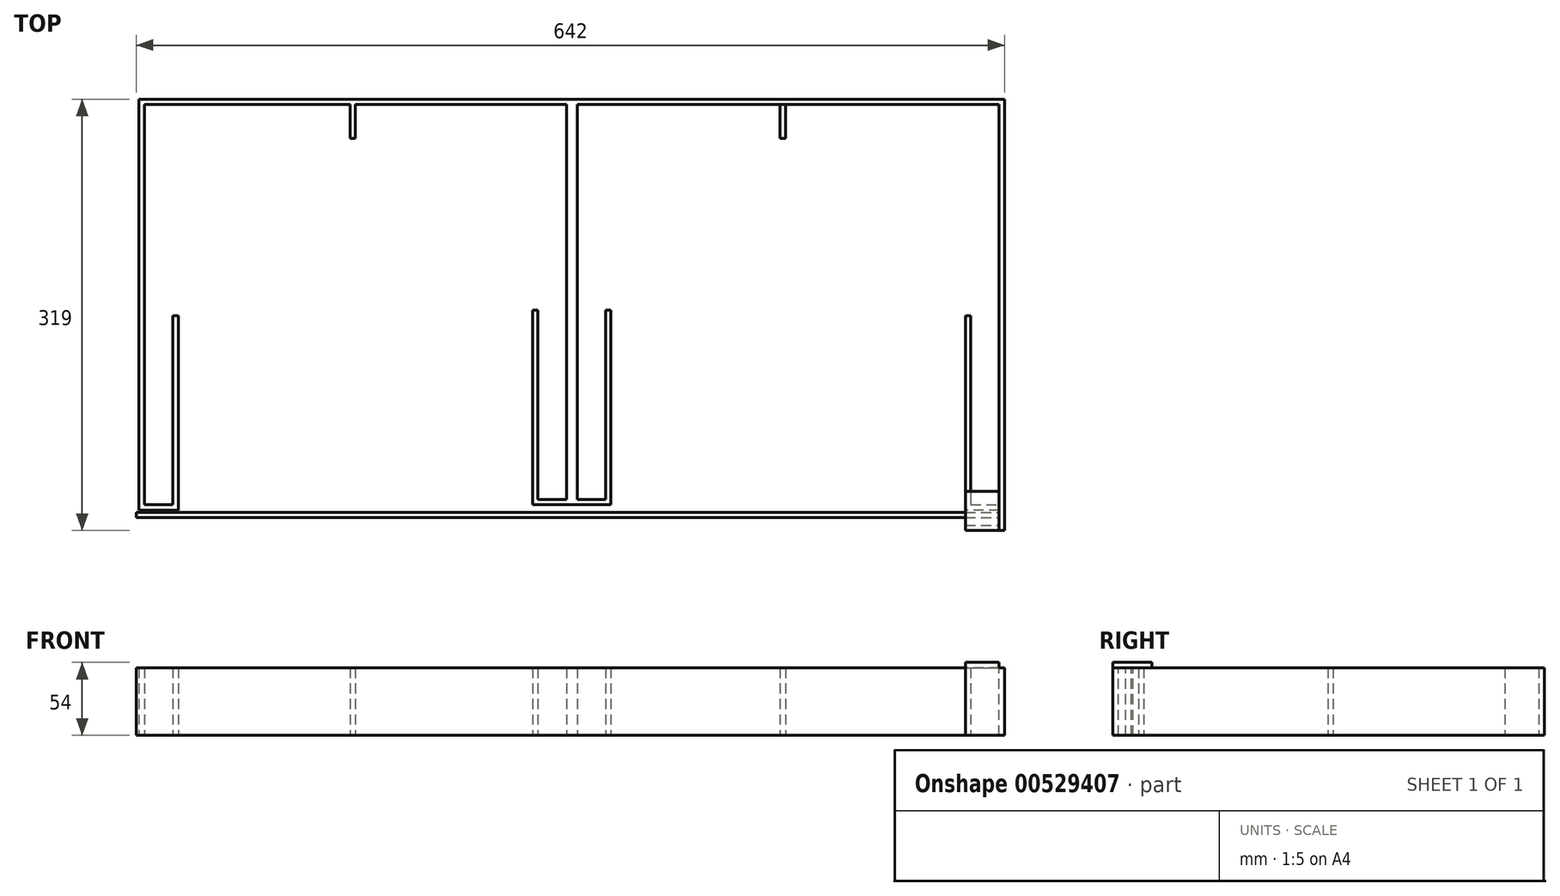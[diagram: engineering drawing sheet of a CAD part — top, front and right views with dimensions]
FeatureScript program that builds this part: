
annotation { "Feature Type Name" : "Feature", "Feature Type Description" : "" }
export const myFeature = defineFeature(function(context is Context, id is Id, definition is map)
    precondition{}
    {
        {
            var Q0;
            Q0=qCreatedBy(makeId("Front.planeOp"),FACE);
            var sketch = newSketch(context, id + "F0", { "sketchPlane" : qUnion([Q0])});
            skLineSegment(sketch, "E0.bottom", {"start": v(320, 25) * mm, "end": v(-320, 25) * mm});
            skLineSegment(sketch, "E0.top", {"start": v(320, -25) * mm, "end": v(-320, -25) * mm});
            skLineSegment(sketch, "E0.left", {"start": v(320, 25) * mm, "end": v(320, -25) * mm});
            skLineSegment(sketch, "E0.right", {"start": v(-320, 25) * mm, "end": v(-320, -25) * mm});
            skPoint(sketch, "E0.middle", {"position": v(0, 0) * mm});
            skSolve(sketch);
        }
        {
            var Q0;
            Q0=makeQuery(id+"F0.imprint","IMPRINT",FACE,{"disambiguationData":[TD([[makeQuery(id+"F0.imprint","IMPRINT",EDGE,{"derivedFrom":sQuery(id+"F0.wireOp",EDGE,"E0.bottom")}),1.0]])]});
            extrude(context, id + "F1", {"entities" : qUnion([Q0]), "depth" : 4 * mm, "offsetDistance" : 25 * mm});
        }
        {
            var Q0;
            Q0=makeQuery(id+"F1.opExtrude","CAP_FACE",FACE,{"disambiguationData":[OSD([sQuery(id+"F0.wireOp",EDGE,"E0.bottom"),sQuery(id+"F0.wireOp",EDGE,"E0.top"),sQuery(id+"F0.wireOp",EDGE,"E0.left"),sQuery(id+"F0.wireOp",EDGE,"E0.right")])],"isStart":false});
            var sketch = newSketch(context, id + "F2", { "sketchPlane" : qUnion([Q0])});
            skLineSegment(sketch, "E1.bottom", {"start": v(-320, 25) * mm, "end": v(-316, 25) * mm});
            skLineSegment(sketch, "E1.top", {"start": v(-320, -25) * mm, "end": v(-316, -25) * mm});
            skLineSegment(sketch, "E1.left", {"start": v(-320, 25) * mm, "end": v(-320, -25) * mm});
            skLineSegment(sketch, "E1.right", {"start": v(-316, 25) * mm, "end": v(-316, -25) * mm});
            skSolve(sketch);
        }
        {
            var Q0;
            Q0 = qSketchRegion(id + "F2", true);
            extrude(context, id + "F3", {"entities" : qUnion([Q0]), "operationType" : NewBodyOperationType.ADD, "depth" : 300 * mm, "offsetDistance" : 25 * mm});
        }
        {
            var Q0;
            Q0=makeQuery(id+"F1.opExtrude","CAP_FACE",FACE,{"disambiguationData":[OSD([sQuery(id+"F0.wireOp",EDGE,"E0.bottom"),sQuery(id+"F0.wireOp",EDGE,"E0.top"),sQuery(id+"F0.wireOp",EDGE,"E0.left"),sQuery(id+"F0.wireOp",EDGE,"E0.right")])],"isStart":false});
            var sketch = newSketch(context, id + "F4", { "sketchPlane" : qUnion([Q0])});
            skLineSegment(sketch, "E2.bottom", {"start": v(320, -25) * mm, "end": v(316, -25) * mm});
            skLineSegment(sketch, "E2.top", {"start": v(320, 25) * mm, "end": v(316, 25) * mm});
            skLineSegment(sketch, "E2.left", {"start": v(320, -25) * mm, "end": v(320, 25) * mm});
            skLineSegment(sketch, "E2.right", {"start": v(316, -25) * mm, "end": v(316, 25) * mm});
            skSolve(sketch);
        }
        {
            var Q0;
            Q0 = qSketchRegion(id + "F4", true);
            extrude(context, id + "F5", {"entities" : qUnion([Q0]), "operationType" : NewBodyOperationType.ADD, "depth" : 300 * mm, "offsetDistance" : 25 * mm});
        }
        {
            var Q0;
            Q0=makeQuery(id+"F3.opExtrude","SWEPT_FACE",FACE,{"disambiguationData":[OSD([sQuery(id+"F2.wireOp",EDGE,"E1.right")])]});
            var sketch = newSketch(context, id + "F6", { "sketchPlane" : qUnion([Q0])});
            skLineSegment(sketch, "E3.bottom", {"start": v(-304, 25) * mm, "end": v(-300, 25) * mm});
            skLineSegment(sketch, "E3.top", {"start": v(-304, -25) * mm, "end": v(-300, -25) * mm});
            skLineSegment(sketch, "E3.left", {"start": v(-304, 25) * mm, "end": v(-304, -25) * mm});
            skLineSegment(sketch, "E3.right", {"start": v(-300, 25) * mm, "end": v(-300, -25) * mm});
            skSolve(sketch);
        }
        {
            var Q0;
            Q0 = qSketchRegion(id + "F6", true);
            extrude(context, id + "F7", {"entities" : qUnion([Q0]), "operationType" : NewBodyOperationType.ADD, "depth" : 25 * mm, "offsetDistance" : 25 * mm});
        }
        {
            var Q0;
            Q0=makeQuery(id+"F5.opExtrude","SWEPT_FACE",FACE,{"disambiguationData":[OSD([sQuery(id+"F4.wireOp",EDGE,"E2.right")])]});
            var sketch = newSketch(context, id + "F8", { "sketchPlane" : qUnion([Q0])});
            skLineSegment(sketch, "E4.bottom", {"start": v(304, 25) * mm, "end": v(300, 25) * mm});
            skLineSegment(sketch, "E4.top", {"start": v(304, -25) * mm, "end": v(300, -25) * mm});
            skLineSegment(sketch, "E4.left", {"start": v(304, 25) * mm, "end": v(304, -25) * mm});
            skLineSegment(sketch, "E4.right", {"start": v(300, 25) * mm, "end": v(300, -25) * mm});
            skSolve(sketch);
        }
        {
            var Q0;
            Q0 = qSketchRegion(id + "F8", true);
            extrude(context, id + "F9", {"entities" : qUnion([Q0]), "operationType" : NewBodyOperationType.ADD, "depth" : 25 * mm, "offsetDistance" : 25 * mm});
        }
        {
            var Q0;
            Q0=qCreatedBy(makeId("Front.planeOp"),FACE);
            var sketch = newSketch(context, id + "F10", { "sketchPlane" : qUnion([Q0])});
            skLineSegment(sketch, "E5.bottom", {"start": v(4, 25) * mm, "end": v(-4, 25) * mm});
            skLineSegment(sketch, "E5.top", {"start": v(4, -25) * mm, "end": v(-4, -25) * mm});
            skLineSegment(sketch, "E5.left", {"start": v(4, 25) * mm, "end": v(4, -25) * mm});
            skLineSegment(sketch, "E5.right", {"start": v(-4, 25) * mm, "end": v(-4, -25) * mm});
            skPoint(sketch, "E5.middle", {"position": v(0, 0) * mm});
            skSolve(sketch);
        }
        {
            var Q0;
            Q0 = qSketchRegion(id + "F10", true);
            extrude(context, id + "F11", {"entities" : qUnion([Q0]), "operationType" : NewBodyOperationType.ADD, "depth" : 300 * mm, "offsetDistance" : 25 * mm});
        }
        {
            var Q0;
            {var subQ0=sQuery(id+"F0.wireOp",EDGE,"E0.bottom");var subQ1=sQuery(id+"F0.wireOp",EDGE,"E0.top");Q0=makeQuery(id+"F11.boolean.opBoolean","SPLIT",FACE,{"disambiguationData":[TD([makeQuery(id+"F3.opExtrude","SWEPT_FACE",FACE,{"disambiguationData":[OSD([sQuery(id+"F2.wireOp",EDGE,"E1.right")])]})])],"derivedFrom":makeQuery(id+"F1.opExtrude","CAP_FACE",FACE,{"disambiguationData":[OSD([subQ0,subQ1,sQuery(id+"F0.wireOp",EDGE,"E0.left"),sQuery(id+"F0.wireOp",EDGE,"E0.right")])],"isStart":false})});}
            var sketch = newSketch(context, id + "F12", { "sketchPlane" : qUnion([Q0])});
            skLineSegment(sketch, "E6.bottom", {"start": v(-160, 25) * mm, "end": v(-164, 25) * mm});
            skLineSegment(sketch, "E6.top", {"start": v(-160, -25) * mm, "end": v(-164, -25) * mm});
            skLineSegment(sketch, "E6.left", {"start": v(-160, 25) * mm, "end": v(-160, -25) * mm});
            skLineSegment(sketch, "E6.right", {"start": v(-164, 25) * mm, "end": v(-164, -25) * mm});
            skSolve(sketch);
        }
        {
            var Q0;
            Q0=makeQuery(id+"F12.imprint","IMPRINT",FACE,{"disambiguationData":[TD([[makeQuery(id+"F12.imprint","IMPRINT",EDGE,{"derivedFrom":sQuery(id+"F12.wireOp",EDGE,"E6.bottom")}),1.0]])]});
            extrude(context, id + "F13", {"entities" : qUnion([Q0]), "operationType" : NewBodyOperationType.ADD, "depth" : 25 * mm, "offsetDistance" : 25 * mm});
        }
        {
            var Q0;
            Q0=makeQuery(id+"F11.opExtrude","SWEPT_FACE",FACE,{"disambiguationData":[OSD([sQuery(id+"F10.wireOp",EDGE,"E5.right")])]});
            var sketch = newSketch(context, id + "F14", { "sketchPlane" : qUnion([Q0])});
            skLineSegment(sketch, "E7.bottom", {"start": v(300, 25) * mm, "end": v(296, 25) * mm});
            skLineSegment(sketch, "E7.top", {"start": v(300, -25) * mm, "end": v(296, -25) * mm});
            skLineSegment(sketch, "E7.left", {"start": v(300, 25) * mm, "end": v(300, -25) * mm});
            skLineSegment(sketch, "E7.right", {"start": v(296, 25) * mm, "end": v(296, -25) * mm});
            skSolve(sketch);
        }
        {
            var Q0;
            Q0 = qSketchRegion(id + "F14", true);
            extrude(context, id + "F15", {"entities" : qUnion([Q0]), "operationType" : NewBodyOperationType.ADD, "depth" : 25 * mm, "offsetDistance" : 25 * mm});
        }
        {
            var Q0;
            Q0=makeQuery(id+"F7.opExtrude","SWEPT_FACE",FACE,{"disambiguationData":[OSD([sQuery(id+"F6.wireOp",EDGE,"E3.right")])]});
            var sketch = newSketch(context, id + "F16", { "sketchPlane" : qUnion([Q0])});
            skLineSegment(sketch, "E8.bottom", {"start": v(291, 25) * mm, "end": v(295, 25) * mm});
            skLineSegment(sketch, "E8.top", {"start": v(291, -25) * mm, "end": v(295, -25) * mm});
            skLineSegment(sketch, "E8.left", {"start": v(291, 25) * mm, "end": v(291, -25) * mm});
            skLineSegment(sketch, "E8.right", {"start": v(295, 25) * mm, "end": v(295, -25) * mm});
            skSolve(sketch);
        }
        {
            var Q0;
            Q0 = qSketchRegion(id + "F16", true);
            extrude(context, id + "F17", {"entities" : qUnion([Q0]), "operationType" : NewBodyOperationType.ADD, "depth" : 140 * mm, "offsetDistance" : 25 * mm});
        }
        {
            var Q0;
            Q0=makeQuery(id+"F15.opExtrude","SWEPT_FACE",FACE,{"disambiguationData":[OSD([sQuery(id+"F14.wireOp",EDGE,"E7.right")])]});
            var sketch = newSketch(context, id + "F18", { "sketchPlane" : qUnion([Q0])});
            skLineSegment(sketch, "E9.bottom", {"start": v(29, 25) * mm, "end": v(25, 25) * mm});
            skLineSegment(sketch, "E9.top", {"start": v(29, -25) * mm, "end": v(25, -25) * mm});
            skLineSegment(sketch, "E9.left", {"start": v(29, 25) * mm, "end": v(29, -25) * mm});
            skLineSegment(sketch, "E9.right", {"start": v(25, 25) * mm, "end": v(25, -25) * mm});
            skSolve(sketch);
        }
        {
            var Q0;
            Q0 = qSketchRegion(id + "F18", true);
            extrude(context, id + "F19", {"entities" : qUnion([Q0]), "operationType" : NewBodyOperationType.ADD, "depth" : 140 * mm, "offsetDistance" : 25 * mm});
        }
        {
            var Q0;
            Q0=makeQuery(id+"F19.boolean.opBoolean","MERGE",FACE,{"derivedFrom":[makeQuery(id+"F17.boolean.opBoolean","MERGE",FACE,{"derivedFrom":[makeQuery(id+"F15.boolean.opBoolean","MERGE",FACE,{"derivedFrom":[makeQuery(id+"F13.boolean.opBoolean","MERGE",FACE,{"derivedFrom":[makeQuery(id+"F11.boolean.opBoolean","MERGE",FACE,{"derivedFrom":[makeQuery(id+"F9.boolean.opBoolean","MERGE",FACE,{"derivedFrom":[makeQuery(id+"F7.boolean.opBoolean","MERGE",FACE,{"derivedFrom":[makeQuery(id+"F5.boolean.opBoolean","MERGE",FACE,{"derivedFrom":[makeQuery(id+"F3.boolean.opBoolean","MERGE",FACE,{"derivedFrom":[makeQuery(id+"F1.opExtrude","SWEPT_FACE",FACE,{"disambiguationData":[OSD([sQuery(id+"F0.wireOp",EDGE,"E0.bottom")])]}),makeQuery(id+"F3.opExtrude","SWEPT_FACE",FACE,{"disambiguationData":[OSD([sQuery(id+"F2.wireOp",EDGE,"E1.bottom")])]})]}),makeQuery(id+"F5.opExtrude","SWEPT_FACE",FACE,{"disambiguationData":[OSD([sQuery(id+"F4.wireOp",EDGE,"E2.top")])]})]}),makeQuery(id+"F7.opExtrude","SWEPT_FACE",FACE,{"disambiguationData":[OSD([sQuery(id+"F6.wireOp",EDGE,"E3.bottom")])]})]}),makeQuery(id+"F9.opExtrude","SWEPT_FACE",FACE,{"disambiguationData":[OSD([sQuery(id+"F8.wireOp",EDGE,"E4.bottom")])]})]}),makeQuery(id+"F11.opExtrude","SWEPT_FACE",FACE,{"disambiguationData":[OSD([sQuery(id+"F10.wireOp",EDGE,"E5.bottom")])]})]}),makeQuery(id+"F13.opExtrude","SWEPT_FACE",FACE,{"disambiguationData":[OSD([sQuery(id+"F12.wireOp",EDGE,"E6.bottom")])]})]}),makeQuery(id+"F15.opExtrude","SWEPT_FACE",FACE,{"disambiguationData":[OSD([sQuery(id+"F14.wireOp",EDGE,"E7.bottom")])]})]}),makeQuery(id+"F17.opExtrude","SWEPT_FACE",FACE,{"disambiguationData":[OSD([sQuery(id+"F16.wireOp",EDGE,"E8.bottom")])]})]}),makeQuery(id+"F19.opExtrude","SWEPT_FACE",FACE,{"disambiguationData":[OSD([sQuery(id+"F18.wireOp",EDGE,"E9.bottom")])]})]});
            var sketch = newSketch(context, id + "F20", { "sketchPlane" : qUnion([Q0])});
            skArc(sketch, "E10", {"start": v(-25, -156) * mm, "mid": v(-161.91, -28.95) * mm, "end": v(-295, -160) * mm});
            skArc(sketch, "E11", {"start": v(-29, -156) * mm, "mid": v(-161.91, -32.85) * mm, "end": v(-291, -160) * mm});
            skSolve(sketch);
        }
        {
            var Q0;
            Q0=sQuery(id+"F20.wireOp",EDGE,"E11");
            var Q1;
            Q1=sQuery(id+"F20.wireOp",EDGE,"E10");
            extrude(context, id + "F21", {"bodyType" : ToolBodyType.SURFACE, "surfaceEntities" : qUnion([Q0, Q1]), "oppositeDirection" : true, "depth" : 50 * mm, "offsetDistance" : 25 * mm});
        }
        {
            var Q0;
            Q0=makeQuery(id+"F11.opExtrude","SWEPT_FACE",FACE,{"disambiguationData":[OSD([sQuery(id+"F10.wireOp",EDGE,"E5.left")])]});
            var sketch = newSketch(context, id + "F22", { "sketchPlane" : qUnion([Q0])});
            skLineSegment(sketch, "E12.bottom", {"start": v(-300, 25) * mm, "end": v(-296, 25) * mm});
            skLineSegment(sketch, "E12.top", {"start": v(-300, -25) * mm, "end": v(-296, -25) * mm});
            skLineSegment(sketch, "E12.left", {"start": v(-300, 25) * mm, "end": v(-300, -25) * mm});
            skLineSegment(sketch, "E12.right", {"start": v(-296, 25) * mm, "end": v(-296, -25) * mm});
            skSolve(sketch);
        }
        {
            var Q0;
            Q0 = qSketchRegion(id + "F22", true);
            extrude(context, id + "F23", {"entities" : qUnion([Q0]), "operationType" : NewBodyOperationType.ADD, "depth" : 25 * mm, "offsetDistance" : 25 * mm});
        }
        {
            var Q0;
            Q0=makeQuery(id+"F23.opExtrude","SWEPT_FACE",FACE,{"disambiguationData":[OSD([sQuery(id+"F22.wireOp",EDGE,"E12.right")])]});
            var sketch = newSketch(context, id + "F24", { "sketchPlane" : qUnion([Q0])});
            skLineSegment(sketch, "E13.bottom", {"start": v(-29, 25) * mm, "end": v(-25, 25) * mm});
            skLineSegment(sketch, "E13.top", {"start": v(-29, -25) * mm, "end": v(-25, -25) * mm});
            skLineSegment(sketch, "E13.left", {"start": v(-29, 25) * mm, "end": v(-29, -25) * mm});
            skLineSegment(sketch, "E13.right", {"start": v(-25, 25) * mm, "end": v(-25, -25) * mm});
            skSolve(sketch);
        }
        {
            var Q0;
            Q0 = qSketchRegion(id + "F24", true);
            extrude(context, id + "F25", {"entities" : qUnion([Q0]), "operationType" : NewBodyOperationType.ADD, "depth" : 140 * mm, "offsetDistance" : 25 * mm});
        }
        {
            var Q0;
            Q0=makeQuery(id+"F9.opExtrude","SWEPT_FACE",FACE,{"disambiguationData":[OSD([sQuery(id+"F8.wireOp",EDGE,"E4.right")])]});
            var sketch = newSketch(context, id + "F26", { "sketchPlane" : qUnion([Q0])});
            skLineSegment(sketch, "E14.bottom", {"start": v(-291, 25) * mm, "end": v(-295, 25) * mm});
            skLineSegment(sketch, "E14.top", {"start": v(-291, -25) * mm, "end": v(-295, -25) * mm});
            skLineSegment(sketch, "E14.left", {"start": v(-291, 25) * mm, "end": v(-291, -25) * mm});
            skLineSegment(sketch, "E14.right", {"start": v(-295, 25) * mm, "end": v(-295, -25) * mm});
            skSolve(sketch);
        }
        {
            var Q0;
            Q0 = qSketchRegion(id + "F26", true);
            extrude(context, id + "F27", {"entities" : qUnion([Q0]), "operationType" : NewBodyOperationType.ADD, "depth" : 140 * mm, "offsetDistance" : 25 * mm});
        }
        {
            var Q0;
            Q0=makeQuery(id+"F27.boolean.opBoolean","MERGE",FACE,{"derivedFrom":[makeQuery(id+"F25.boolean.opBoolean","MERGE",FACE,{"derivedFrom":[makeQuery(id+"F23.boolean.opBoolean","MERGE",FACE,{"derivedFrom":[makeQuery(id+"F19.boolean.opBoolean","MERGE",FACE,{"derivedFrom":[makeQuery(id+"F17.boolean.opBoolean","MERGE",FACE,{"derivedFrom":[makeQuery(id+"F15.boolean.opBoolean","MERGE",FACE,{"derivedFrom":[makeQuery(id+"F13.boolean.opBoolean","MERGE",FACE,{"derivedFrom":[makeQuery(id+"F11.boolean.opBoolean","MERGE",FACE,{"derivedFrom":[makeQuery(id+"F9.boolean.opBoolean","MERGE",FACE,{"derivedFrom":[makeQuery(id+"F7.boolean.opBoolean","MERGE",FACE,{"derivedFrom":[makeQuery(id+"F5.boolean.opBoolean","MERGE",FACE,{"derivedFrom":[makeQuery(id+"F3.boolean.opBoolean","MERGE",FACE,{"derivedFrom":[makeQuery(id+"F1.opExtrude","SWEPT_FACE",FACE,{"disambiguationData":[OSD([sQuery(id+"F0.wireOp",EDGE,"E0.top")])]}),makeQuery(id+"F3.opExtrude","SWEPT_FACE",FACE,{"disambiguationData":[OSD([sQuery(id+"F2.wireOp",EDGE,"E1.top")])]})]}),makeQuery(id+"F5.opExtrude","SWEPT_FACE",FACE,{"disambiguationData":[OSD([sQuery(id+"F4.wireOp",EDGE,"E2.bottom")])]})]}),makeQuery(id+"F7.opExtrude","SWEPT_FACE",FACE,{"disambiguationData":[OSD([sQuery(id+"F6.wireOp",EDGE,"E3.top")])]})]}),makeQuery(id+"F9.opExtrude","SWEPT_FACE",FACE,{"disambiguationData":[OSD([sQuery(id+"F8.wireOp",EDGE,"E4.top")])]})]}),makeQuery(id+"F11.opExtrude","SWEPT_FACE",FACE,{"disambiguationData":[OSD([sQuery(id+"F10.wireOp",EDGE,"E5.top")])]})]}),makeQuery(id+"F13.opExtrude","SWEPT_FACE",FACE,{"disambiguationData":[OSD([sQuery(id+"F12.wireOp",EDGE,"E6.top")])]})]}),makeQuery(id+"F15.opExtrude","SWEPT_FACE",FACE,{"disambiguationData":[OSD([sQuery(id+"F14.wireOp",EDGE,"E7.top")])]})]}),makeQuery(id+"F17.opExtrude","SWEPT_FACE",FACE,{"disambiguationData":[OSD([sQuery(id+"F16.wireOp",EDGE,"E8.top")])]})]}),makeQuery(id+"F19.opExtrude","SWEPT_FACE",FACE,{"disambiguationData":[OSD([sQuery(id+"F18.wireOp",EDGE,"E9.top")])]})]}),makeQuery(id+"F23.opExtrude","SWEPT_FACE",FACE,{"disambiguationData":[OSD([sQuery(id+"F22.wireOp",EDGE,"E12.top")])]})]}),makeQuery(id+"F25.opExtrude","SWEPT_FACE",FACE,{"disambiguationData":[OSD([sQuery(id+"F24.wireOp",EDGE,"E13.top")])]})]}),makeQuery(id+"F27.opExtrude","SWEPT_FACE",FACE,{"disambiguationData":[OSD([sQuery(id+"F26.wireOp",EDGE,"E14.top")])]})]});
            var sketch = newSketch(context, id + "F28", { "sketchPlane" : qUnion([Q0])});
            skLineSegment(sketch, "E15", {"start": v(4, 4) * mm, "end": v(154, 4) * mm});
            skLineSegment(sketch, "E16.bottom", {"start": v(154, 4) * mm, "end": v(158, 4) * mm});
            skLineSegment(sketch, "E16.top", {"start": v(154, 29) * mm, "end": v(158, 29) * mm});
            skLineSegment(sketch, "E16.left", {"start": v(154, 4) * mm, "end": v(154, 29) * mm});
            skLineSegment(sketch, "E16.right", {"start": v(158, 4) * mm, "end": v(158, 29) * mm});
            skSolve(sketch);
        }
        {
            var Q0;
            Q0 = qSketchRegion(id + "F28", true);
            extrude(context, id + "F29", {"entities" : qUnion([Q0]), "oppositeDirection" : true, "depth" : 50 * mm, "offsetDistance" : 25 * mm});
        }
        {
            var Q0;
            Q0=makeQuery(id+"F21.opExtrude","SWEPT_BODY",BODY,{"disambiguationData":[OSD([sQuery(id+"F20.wireOp",EDGE,"E10")])]});
            var Q1;
            Q1=makeQuery(id+"F21.opExtrude","SWEPT_BODY",BODY,{"disambiguationData":[OSD([sQuery(id+"F20.wireOp",EDGE,"E11")])]});
            var Q2;
            Q2=qCreatedBy(makeId("Right.planeOp"),FACE);
            mirror(context, id + "F30", {"entities" : qUnion([Q0, Q1]), "mirrorPlane" : qUnion([Q2])});
        }
        {
            var Q0;
            Q0=makeQuery(id+"F9.boolean.opBoolean","MERGE",FACE,{"derivedFrom":[makeQuery(id+"F5.opExtrude","CAP_FACE",FACE,{"disambiguationData":[OSD([sQuery(id+"F4.wireOp",EDGE,"E2.bottom"),sQuery(id+"F4.wireOp",EDGE,"E2.top"),sQuery(id+"F4.wireOp",EDGE,"E2.left"),sQuery(id+"F4.wireOp",EDGE,"E2.right")])],"isStart":false}),makeQuery(id+"F9.opExtrude","SWEPT_FACE",FACE,{"disambiguationData":[OSD([sQuery(id+"F8.wireOp",EDGE,"E4.left")])]})]});
            var sketch = newSketch(context, id + "F31", { "sketchPlane" : qUnion([Q0])});
            skLineSegment(sketch, "E17.bottom", {"start": v(320, -25) * mm, "end": v(316, -25) * mm});
            skLineSegment(sketch, "E17.top", {"start": v(320, 25) * mm, "end": v(316, 25) * mm});
            skLineSegment(sketch, "E17.left", {"start": v(320, -25) * mm, "end": v(320, 25) * mm});
            skLineSegment(sketch, "E17.right", {"start": v(316, -25) * mm, "end": v(316, 25) * mm});
            skSolve(sketch);
        }
        {
            var Q0;
            Q0 = qSketchRegion(id + "F31", true);
            extrude(context, id + "F32", {"entities" : qUnion([Q0]), "operationType" : NewBodyOperationType.ADD, "depth" : 15 * mm, "offsetDistance" : 25 * mm});
        }
        {
            var Q0;
            Q0=makeQuery(id+"F32.opExtrude","SWEPT_FACE",FACE,{"disambiguationData":[OSD([sQuery(id+"F31.wireOp",EDGE,"E17.right")])]});
            var sketch = newSketch(context, id + "F33", { "sketchPlane" : qUnion([Q0])});
            skLineSegment(sketch, "E18.bottom", {"start": v(319, -25) * mm, "end": v(315, -25) * mm});
            skLineSegment(sketch, "E18.top", {"start": v(319, 25) * mm, "end": v(315, 25) * mm});
            skLineSegment(sketch, "E18.left", {"start": v(319, -25) * mm, "end": v(319, 25) * mm});
            skLineSegment(sketch, "E18.right", {"start": v(315, -25) * mm, "end": v(315, 25) * mm});
            skSolve(sketch);
        }
        {
            var Q0;
            Q0 = qSketchRegion(id + "F33", true);
            extrude(context, id + "F34", {"entities" : qUnion([Q0]), "operationType" : NewBodyOperationType.ADD, "depth" : 25 * mm, "offsetDistance" : 25 * mm});
        }
        {
            var Q0;
            Q0=makeQuery(id+"F34.boolean.opBoolean","MERGE",FACE,{"derivedFrom":[makeQuery(id+"F32.boolean.opBoolean","MERGE",FACE,{"derivedFrom":[makeQuery(id+"F27.boolean.opBoolean","MERGE",FACE,{"derivedFrom":[makeQuery(id+"F25.boolean.opBoolean","MERGE",FACE,{"derivedFrom":[makeQuery(id+"F23.boolean.opBoolean","MERGE",FACE,{"derivedFrom":[makeQuery(id+"F19.boolean.opBoolean","MERGE",FACE,{"derivedFrom":[makeQuery(id+"F17.boolean.opBoolean","MERGE",FACE,{"derivedFrom":[makeQuery(id+"F15.boolean.opBoolean","MERGE",FACE,{"derivedFrom":[makeQuery(id+"F13.boolean.opBoolean","MERGE",FACE,{"derivedFrom":[makeQuery(id+"F11.boolean.opBoolean","MERGE",FACE,{"derivedFrom":[makeQuery(id+"F9.boolean.opBoolean","MERGE",FACE,{"derivedFrom":[makeQuery(id+"F7.boolean.opBoolean","MERGE",FACE,{"derivedFrom":[makeQuery(id+"F5.boolean.opBoolean","MERGE",FACE,{"derivedFrom":[makeQuery(id+"F3.boolean.opBoolean","MERGE",FACE,{"derivedFrom":[makeQuery(id+"F1.opExtrude","SWEPT_FACE",FACE,{"disambiguationData":[OSD([sQuery(id+"F0.wireOp",EDGE,"E0.bottom")])]}),makeQuery(id+"F3.opExtrude","SWEPT_FACE",FACE,{"disambiguationData":[OSD([sQuery(id+"F2.wireOp",EDGE,"E1.bottom")])]})]}),makeQuery(id+"F5.opExtrude","SWEPT_FACE",FACE,{"disambiguationData":[OSD([sQuery(id+"F4.wireOp",EDGE,"E2.top")])]})]}),makeQuery(id+"F7.opExtrude","SWEPT_FACE",FACE,{"disambiguationData":[OSD([sQuery(id+"F6.wireOp",EDGE,"E3.bottom")])]})]}),makeQuery(id+"F9.opExtrude","SWEPT_FACE",FACE,{"disambiguationData":[OSD([sQuery(id+"F8.wireOp",EDGE,"E4.bottom")])]})]}),makeQuery(id+"F11.opExtrude","SWEPT_FACE",FACE,{"disambiguationData":[OSD([sQuery(id+"F10.wireOp",EDGE,"E5.bottom")])]})]}),makeQuery(id+"F13.opExtrude","SWEPT_FACE",FACE,{"disambiguationData":[OSD([sQuery(id+"F12.wireOp",EDGE,"E6.bottom")])]})]}),makeQuery(id+"F15.opExtrude","SWEPT_FACE",FACE,{"disambiguationData":[OSD([sQuery(id+"F14.wireOp",EDGE,"E7.bottom")])]})]}),makeQuery(id+"F17.opExtrude","SWEPT_FACE",FACE,{"disambiguationData":[OSD([sQuery(id+"F16.wireOp",EDGE,"E8.bottom")])]})]}),makeQuery(id+"F19.opExtrude","SWEPT_FACE",FACE,{"disambiguationData":[OSD([sQuery(id+"F18.wireOp",EDGE,"E9.bottom")])]})]}),makeQuery(id+"F23.opExtrude","SWEPT_FACE",FACE,{"disambiguationData":[OSD([sQuery(id+"F22.wireOp",EDGE,"E12.bottom")])]})]}),makeQuery(id+"F25.opExtrude","SWEPT_FACE",FACE,{"disambiguationData":[OSD([sQuery(id+"F24.wireOp",EDGE,"E13.bottom")])]})]}),makeQuery(id+"F27.opExtrude","SWEPT_FACE",FACE,{"disambiguationData":[OSD([sQuery(id+"F26.wireOp",EDGE,"E14.bottom")])]})]}),makeQuery(id+"F32.opExtrude","SWEPT_FACE",FACE,{"disambiguationData":[OSD([sQuery(id+"F31.wireOp",EDGE,"E17.top")])]})]}),makeQuery(id+"F34.opExtrude","SWEPT_FACE",FACE,{"disambiguationData":[OSD([sQuery(id+"F33.wireOp",EDGE,"E18.top")])]})]});
            var sketch = newSketch(context, id + "F35", { "sketchPlane" : qUnion([Q0])});
            skLineSegment(sketch, "E19.bottom", {"start": v(291, -319) * mm, "end": v(316, -319) * mm});
            skLineSegment(sketch, "E19.top", {"start": v(291, -315) * mm, "end": v(316, -315) * mm});
            skLineSegment(sketch, "E19.left", {"start": v(291, -319) * mm, "end": v(291, -315) * mm});
            skLineSegment(sketch, "E19.right", {"start": v(316, -319) * mm, "end": v(316, -315) * mm});
            skSolve(sketch);
        }
        {
            var Q0;
            Q0 = qSketchRegion(id + "F35", true);
            extrude(context, id + "F36", {"entities" : qUnion([Q0]), "operationType" : NewBodyOperationType.ADD, "depth" : 4 * mm, "offsetDistance" : 25 * mm});
        }
        {
            var Q0;
            Q0=makeQuery(id+"F36.boolean.opBoolean","MERGE",FACE,{"derivedFrom":[makeQuery(id+"F34.opExtrude","SWEPT_FACE",FACE,{"disambiguationData":[OSD([sQuery(id+"F33.wireOp",EDGE,"E18.right")])]}),makeQuery(id+"F36.opExtrude","SWEPT_FACE",FACE,{"disambiguationData":[OSD([sQuery(id+"F35.wireOp",EDGE,"E19.top")])]})]});
            var sketch = newSketch(context, id + "F37", { "sketchPlane" : qUnion([Q0])});
            skLineSegment(sketch, "E20.bottom", {"start": v(-291, 29) * mm, "end": v(-316, 29) * mm});
            skLineSegment(sketch, "E20.top", {"start": v(-291, 25.1) * mm, "end": v(-316, 25.1) * mm});
            skLineSegment(sketch, "E20.left", {"start": v(-291, 29) * mm, "end": v(-291, 25.1) * mm});
            skLineSegment(sketch, "E20.right", {"start": v(-316, 29) * mm, "end": v(-316, 25.1) * mm});
            skSolve(sketch);
        }
        {
            var Q0;
            Q0 = qSketchRegion(id + "F37", true);
            extrude(context, id + "F38", {"entities" : qUnion([Q0]), "operationType" : NewBodyOperationType.ADD, "depth" : 25 * mm, "offsetDistance" : 25 * mm});
        }
        {
            var Q0;
            Q0=makeQuery(id+"F32.opExtrude","SWEPT_FACE",FACE,{"disambiguationData":[OSD([sQuery(id+"F31.wireOp",EDGE,"E17.right")])]});
            var sketch = newSketch(context, id + "F39", { "sketchPlane" : qUnion([Q0])});
            skLineSegment(sketch, "E21.bottom", {"start": v(309.5, -25) * mm, "end": v(305.5, -25) * mm});
            skLineSegment(sketch, "E21.top", {"start": v(309.5, 25) * mm, "end": v(305.5, 25) * mm});
            skLineSegment(sketch, "E21.left", {"start": v(309.5, -25) * mm, "end": v(309.5, 25) * mm});
            skLineSegment(sketch, "E21.right", {"start": v(305.5, -25) * mm, "end": v(305.5, 25) * mm});
            skSolve(sketch);
        }
        {
            var Q0;
            Q0 = qSketchRegion(id + "F39", true);
            extrude(context, id + "F40", {"entities" : qUnion([Q0]), "operationType" : NewBodyOperationType.ADD, "depth" : 638 * mm, "offsetDistance" : 25 * mm});
        }
    });
